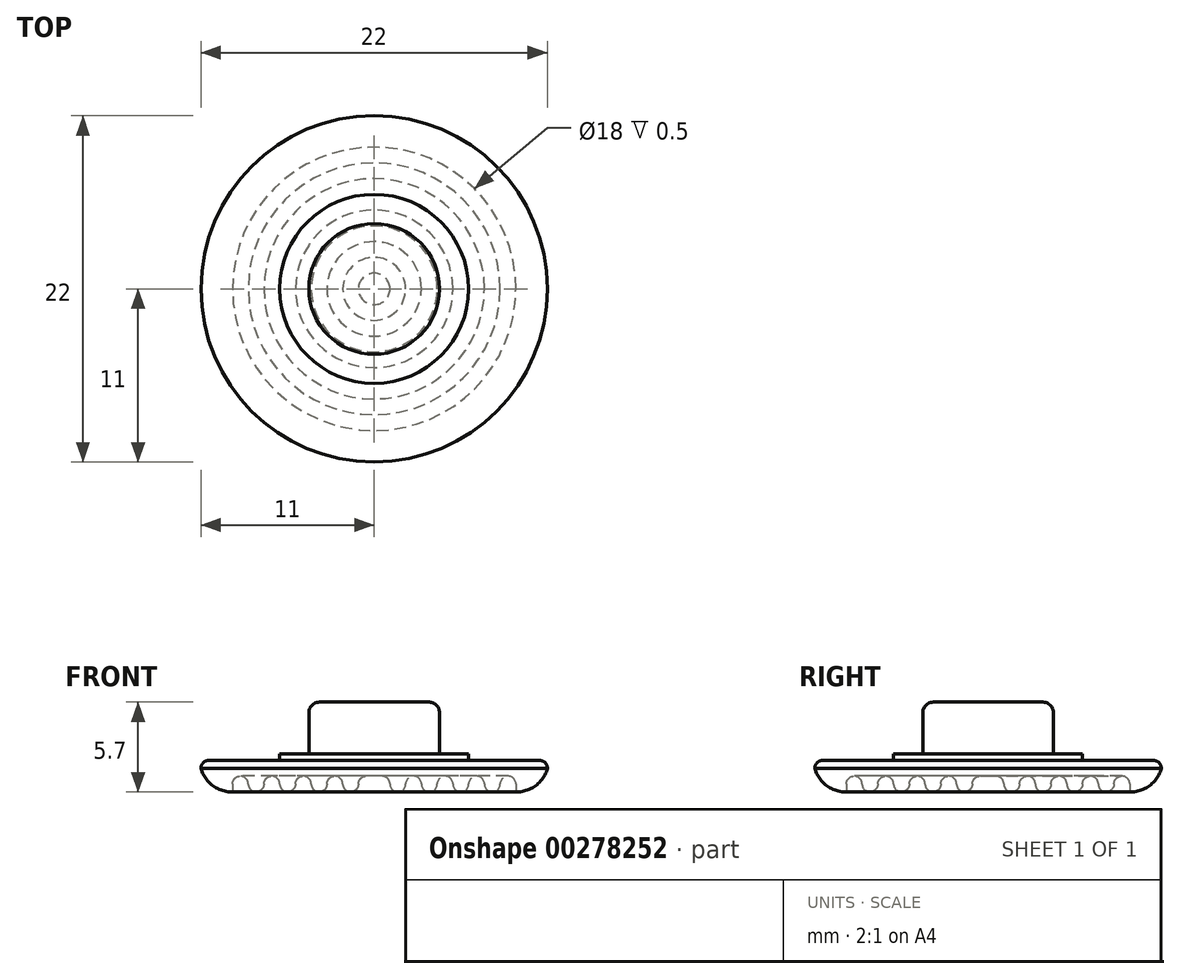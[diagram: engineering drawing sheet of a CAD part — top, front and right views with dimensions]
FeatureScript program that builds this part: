
annotation { "Feature Type Name" : "Feature", "Feature Type Description" : "" }
export const myFeature = defineFeature(function(context is Context, id is Id, definition is map)
    precondition{}
    {
        {
            var Q0;
            Q0=qCreatedBy(makeId("Top.planeOp"),FACE);
            var sketch = newSketch(context, id + "F0", { "sketchPlane" : qUnion([Q0])});
            skCircle(sketch, "E0", {"center": v(0, 0) * mm, "radius": 4.15 * mm});
            skCircle(sketch, "E1", {"center": v(0, 0) * mm, "radius": 11 * mm});
            skCircle(sketch, "E2", {"center": v(0, 0) * mm, "radius": 6 * mm});
            skSolve(sketch);
        }
        {
            var Q0;
            Q0=makeQuery(id+"F0.imprint","IMPRINT",FACE,{"disambiguationData":[TD([[makeQuery(id+"F0.imprint","IMPRINT",EDGE,{"derivedFrom":sQuery(id+"F0.wireOp",EDGE,"E0")}),-1.0]])]});
            var Q1;
            Q1=makeQuery(id+"F0.imprint","IMPRINT",FACE,{"disambiguationData":[TD([[makeQuery(id+"F0.imprint","IMPRINT",EDGE,{"derivedFrom":sQuery(id+"F0.wireOp",EDGE,"E0")}),1.0]])]});
            var Q2;
            Q2=makeQuery(id+"F0.imprint","IMPRINT",FACE,{"disambiguationData":[TD([[makeQuery(id+"F0.imprint","IMPRINT",EDGE,{"derivedFrom":sQuery(id+"F0.wireOp",EDGE,"E1")}),1.0]])]});
            extrude(context, id + "F1", {"entities" : qUnion([Q0, Q1, Q2]), "depth" : 2 * mm, "offsetDistance" : 25 * mm});
        }
        {
            var Q0;
            Q0=makeQuery(id+"F0.imprint","IMPRINT",FACE,{"disambiguationData":[TD([[makeQuery(id+"F0.imprint","IMPRINT",EDGE,{"derivedFrom":sQuery(id+"F0.wireOp",EDGE,"E0")}),1.0]])]});
            extrude(context, id + "F2", {"entities" : qUnion([Q0]), "operationType" : NewBodyOperationType.ADD, "depth" : 5.7 * mm, "offsetDistance" : 25 * mm});
        }
        {
            var Q0;
            Q0=makeQuery(id+"F1.opExtrude","CAP_EDGE",EDGE,{"disambiguationData":[OSD([sQuery(id+"F0.wireOp",EDGE,"E1")])],"isStart":false});
            fillet(context, id + "F3", {"entities" : qUnion([Q0]), "radius" : .5 * mm, "tangentPropagation" : true, "allowEdgeOverflow" : false});
        }
        {
            var Q0;
            Q0=makeQuery(id+"F1.opExtrude","CAP_EDGE",EDGE,{"disambiguationData":[OSD([sQuery(id+"F0.wireOp",EDGE,"E1")])],"isStart":true});
            fillet(context, id + "F4", {"entities" : qUnion([Q0]), "radius" : 2 * mm, "tangentPropagation" : true, "allowEdgeOverflow" : false});
        }
        {
            var Q0;
            Q0=makeQuery(id+"F0.imprint","IMPRINT",FACE,{"disambiguationData":[TD([[makeQuery(id+"F0.imprint","IMPRINT",EDGE,{"derivedFrom":sQuery(id+"F0.wireOp",EDGE,"E0")}),-1.0]])]});
            extrude(context, id + "F5", {"entities" : qUnion([Q0]), "operationType" : NewBodyOperationType.ADD, "depth" : 2.4 * mm, "offsetDistance" : 25 * mm});
        }
        {
            var Q0;
            Q0=qCreatedBy(makeId("Top.planeOp"),FACE);
            var sketch = newSketch(context, id + "F6", { "sketchPlane" : qUnion([Q0])});
            skCircle(sketch, "E3", {"center": v(0, 0) * mm, "radius": 11 * mm});
            skCircle(sketch, "E4", {"center": v(0, 0) * mm, "radius": 8 * mm});
            skCircle(sketch, "E5", {"center": v(0, 0) * mm, "radius": 7.5 * mm});
            skCircle(sketch, "E6", {"center": v(0, 0) * mm, "radius": 7 * mm});
            skCircle(sketch, "E7", {"center": v(0, 0) * mm, "radius": 6 * mm});
            skCircle(sketch, "E8", {"center": v(0, 0) * mm, "radius": 5.5 * mm});
            skCircle(sketch, "E9", {"center": v(0, 0) * mm, "radius": 5 * mm});
            skCircle(sketch, "E10", {"center": v(0, 0) * mm, "radius": 4.5 * mm});
            skCircle(sketch, "E11", {"center": v(0, 0) * mm, "radius": 4 * mm});
            skCircle(sketch, "E12", {"center": v(0, 0) * mm, "radius": 3.5 * mm});
            skCircle(sketch, "E13", {"center": v(0, 0) * mm, "radius": 3 * mm});
            skCircle(sketch, "E14", {"center": v(0, 0) * mm, "radius": 2.5 * mm});
            skCircle(sketch, "E15", {"center": v(0, 0) * mm, "radius": 2 * mm});
            skCircle(sketch, "E16", {"center": v(0, 0) * mm, "radius": 1.5 * mm});
            skCircle(sketch, "E17", {"center": v(0, 0) * mm, "radius": 1 * mm});
            skCircle(sketch, "E18", {"center": v(0, 0) * mm, "radius": 0.5 * mm});
            skCircle(sketch, "E19", {"center": v(0, 0) * mm, "radius": 6.5 * mm});
            skCircle(sketch, "E20", {"center": v(0, 0) * mm, "radius": 8.5 * mm});
            skCircle(sketch, "E21", {"center": v(0, 0) * mm, "radius": 9 * mm});
            skSolve(sketch);
        }
        {
            var Q0;
            Q0=makeQuery(id+"F6.imprint","IMPRINT",FACE,{"disambiguationData":[TD([[makeQuery(id+"F6.imprint","IMPRINT",EDGE,{"derivedFrom":sQuery(id+"F6.wireOp",EDGE,"E18")}),1.0]])]});
            var Q1;
            Q1=makeQuery(id+"F6.imprint","IMPRINT",FACE,{"disambiguationData":[TD([[makeQuery(id+"F6.imprint","IMPRINT",EDGE,{"derivedFrom":sQuery(id+"F6.wireOp",EDGE,"E14")}),1.0]])]});
            var Q2;
            Q2=makeQuery(id+"F6.imprint","IMPRINT",FACE,{"disambiguationData":[TD([[makeQuery(id+"F6.imprint","IMPRINT",EDGE,{"derivedFrom":sQuery(id+"F6.wireOp",EDGE,"E10")}),1.0]])]});
            var Q3;
            Q3=makeQuery(id+"F6.imprint","IMPRINT",FACE,{"disambiguationData":[TD([[makeQuery(id+"F6.imprint","IMPRINT",EDGE,{"derivedFrom":sQuery(id+"F6.wireOp",EDGE,"E7")}),-1.0]])]});
            var Q4;
            Q4=makeQuery(id+"F6.imprint","IMPRINT",FACE,{"disambiguationData":[TD([[makeQuery(id+"F6.imprint","IMPRINT",EDGE,{"derivedFrom":sQuery(id+"F6.wireOp",EDGE,"E17")}),1.0]])]});
            var Q5;
            Q5=makeQuery(id+"F6.imprint","IMPRINT",FACE,{"disambiguationData":[TD([[makeQuery(id+"F6.imprint","IMPRINT",EDGE,{"derivedFrom":sQuery(id+"F6.wireOp",EDGE,"E13")}),1.0]])]});
            var Q6;
            Q6=makeQuery(id+"F6.imprint","IMPRINT",FACE,{"disambiguationData":[TD([[makeQuery(id+"F6.imprint","IMPRINT",EDGE,{"derivedFrom":sQuery(id+"F6.wireOp",EDGE,"E9")}),1.0]])]});
            var Q7;
            Q7=makeQuery(id+"F6.imprint","IMPRINT",FACE,{"disambiguationData":[TD([[makeQuery(id+"F6.imprint","IMPRINT",EDGE,{"derivedFrom":sQuery(id+"F6.wireOp",EDGE,"E6")}),1.0]])]});
            var Q8;
            Q8=makeQuery(id+"F6.imprint","IMPRINT",FACE,{"disambiguationData":[TD([[makeQuery(id+"F6.imprint","IMPRINT",EDGE,{"derivedFrom":sQuery(id+"F6.wireOp",EDGE,"E20")}),-1.0]])]});
            var Q9;
            Q9=makeQuery(id+"F6.imprint","IMPRINT",FACE,{"disambiguationData":[TD([[makeQuery(id+"F6.imprint","IMPRINT",EDGE,{"derivedFrom":sQuery(id+"F6.wireOp",EDGE,"E4")}),-1.0]])]});
            extrude(context, id + "F7", {"entities" : qUnion([Q0, Q1, Q2, Q3, Q4, Q5, Q6, Q7, Q8, Q9]), "operationType" : NewBodyOperationType.REMOVE, "depth" : 1 * mm, "offsetDistance" : 25 * mm});
        }
        {
            var Q0;
            Q0=makeQuery(id+"F7.boolean.opBoolean","COPY",FACE,{"derivedFrom":makeQuery(id+"F7.opExtrude","CAP_FACE",FACE,{"disambiguationData":[OSD([sQuery(id+"F6.wireOp",EDGE,"E16"),sQuery(id+"F6.wireOp",EDGE,"E17")])],"isStart":false})});
            var Q1;
            Q1=makeQuery(id+"F7.boolean.opBoolean","COPY",FACE,{"derivedFrom":makeQuery(id+"F7.opExtrude","CAP_FACE",FACE,{"disambiguationData":[OSD([sQuery(id+"F6.wireOp",EDGE,"E14"),sQuery(id+"F6.wireOp",EDGE,"E15")])],"isStart":false})});
            var Q2;
            Q2=makeQuery(id+"F7.boolean.opBoolean","COPY",FACE,{"derivedFrom":makeQuery(id+"F7.opExtrude","CAP_FACE",FACE,{"disambiguationData":[OSD([sQuery(id+"F6.wireOp",EDGE,"E18")])],"isStart":false})});
            var Q3;
            Q3=makeQuery(id+"F7.boolean.opBoolean","COPY",FACE,{"derivedFrom":makeQuery(id+"F7.opExtrude","CAP_FACE",FACE,{"disambiguationData":[OSD([sQuery(id+"F6.wireOp",EDGE,"E12"),sQuery(id+"F6.wireOp",EDGE,"E13")])],"isStart":false})});
            var Q4;
            Q4=makeQuery(id+"F7.boolean.opBoolean","COPY",FACE,{"derivedFrom":makeQuery(id+"F7.opExtrude","CAP_FACE",FACE,{"disambiguationData":[OSD([sQuery(id+"F6.wireOp",EDGE,"E10"),sQuery(id+"F6.wireOp",EDGE,"E11")])],"isStart":false})});
            var Q5;
            Q5=makeQuery(id+"F7.boolean.opBoolean","COPY",FACE,{"derivedFrom":makeQuery(id+"F7.opExtrude","CAP_FACE",FACE,{"disambiguationData":[OSD([sQuery(id+"F6.wireOp",EDGE,"E8"),sQuery(id+"F6.wireOp",EDGE,"E9")])],"isStart":false})});
            var Q6;
            Q6=makeQuery(id+"F7.boolean.opBoolean","COPY",FACE,{"derivedFrom":makeQuery(id+"F7.opExtrude","CAP_FACE",FACE,{"disambiguationData":[OSD([sQuery(id+"F6.wireOp",EDGE,"E7"),sQuery(id+"F6.wireOp",EDGE,"E19")])],"isStart":false})});
            var Q7;
            Q7=makeQuery(id+"F7.boolean.opBoolean","COPY",FACE,{"derivedFrom":makeQuery(id+"F7.opExtrude","CAP_FACE",FACE,{"disambiguationData":[OSD([sQuery(id+"F6.wireOp",EDGE,"E5"),sQuery(id+"F6.wireOp",EDGE,"E6")])],"isStart":false})});
            var Q8;
            Q8=makeQuery(id+"F7.boolean.opBoolean","COPY",FACE,{"derivedFrom":makeQuery(id+"F7.opExtrude","CAP_FACE",FACE,{"disambiguationData":[OSD([sQuery(id+"F6.wireOp",EDGE,"E4"),sQuery(id+"F6.wireOp",EDGE,"E21")])],"isStart":false})});
            fillet(context, id + "F8", {"entities" : qUnion([Q0, Q1, Q2, Q3, Q4, Q5, Q6, Q7, Q8]), "radius" : .5 * mm, "tangentPropagation" : true, "allowEdgeOverflow" : false});
        }
        {
            var Q0;
            Q0=makeQuery(id+"F7.boolean.opBoolean","SPLIT",FACE,{"disambiguationData":[TD([makeQuery(id+"F7.opExtrude","SWEPT_FACE",FACE,{"disambiguationData":[OSD([sQuery(id+"F6.wireOp",EDGE,"E17")])]})])],"derivedFrom":makeQuery(id+"F1.opExtrude","CAP_FACE",FACE,{"disambiguationData":[OSD([sQuery(id+"F0.wireOp",EDGE,"E1")])],"isStart":true})});
            var Q1;
            Q1=makeQuery(id+"F7.boolean.opBoolean","SPLIT",FACE,{"disambiguationData":[TD([makeQuery(id+"F7.opExtrude","SWEPT_FACE",FACE,{"disambiguationData":[OSD([sQuery(id+"F6.wireOp",EDGE,"E15")])]})])],"derivedFrom":makeQuery(id+"F1.opExtrude","CAP_FACE",FACE,{"disambiguationData":[OSD([sQuery(id+"F0.wireOp",EDGE,"E1")])],"isStart":true})});
            var Q2;
            Q2=makeQuery(id+"F7.boolean.opBoolean","SPLIT",FACE,{"disambiguationData":[TD([makeQuery(id+"F7.opExtrude","SWEPT_FACE",FACE,{"disambiguationData":[OSD([sQuery(id+"F6.wireOp",EDGE,"E13")])]})])],"derivedFrom":makeQuery(id+"F1.opExtrude","CAP_FACE",FACE,{"disambiguationData":[OSD([sQuery(id+"F0.wireOp",EDGE,"E1")])],"isStart":true})});
            var Q3;
            Q3=makeQuery(id+"F7.boolean.opBoolean","SPLIT",FACE,{"disambiguationData":[TD([makeQuery(id+"F7.opExtrude","SWEPT_FACE",FACE,{"disambiguationData":[OSD([sQuery(id+"F6.wireOp",EDGE,"E11")])]})])],"derivedFrom":makeQuery(id+"F1.opExtrude","CAP_FACE",FACE,{"disambiguationData":[OSD([sQuery(id+"F0.wireOp",EDGE,"E1")])],"isStart":true})});
            var Q4;
            Q4=makeQuery(id+"F7.boolean.opBoolean","SPLIT",FACE,{"disambiguationData":[TD([makeQuery(id+"F7.opExtrude","SWEPT_FACE",FACE,{"disambiguationData":[OSD([sQuery(id+"F6.wireOp",EDGE,"E8")])]})])],"derivedFrom":makeQuery(id+"F1.opExtrude","CAP_FACE",FACE,{"disambiguationData":[OSD([sQuery(id+"F0.wireOp",EDGE,"E1")])],"isStart":true})});
            var Q5;
            Q5=makeQuery(id+"F7.boolean.opBoolean","SPLIT",FACE,{"disambiguationData":[TD([makeQuery(id+"F7.opExtrude","SWEPT_FACE",FACE,{"disambiguationData":[OSD([sQuery(id+"F6.wireOp",EDGE,"E6")])]})])],"derivedFrom":makeQuery(id+"F1.opExtrude","CAP_FACE",FACE,{"disambiguationData":[OSD([sQuery(id+"F0.wireOp",EDGE,"E1")])],"isStart":true})});
            var Q6;
            Q6=makeQuery(id+"F7.boolean.opBoolean","COPY",EDGE,{"derivedFrom":makeQuery(id+"F7.opExtrude","CAP_EDGE",EDGE,{"disambiguationData":[OSD([sQuery(id+"F6.wireOp",EDGE,"E5")])],"isStart":true})});
            var Q7;
            Q7=makeQuery(id+"F7.boolean.opBoolean","SPLIT",FACE,{"disambiguationData":[TD([makeQuery(id+"F7.opExtrude","SWEPT_FACE",FACE,{"disambiguationData":[OSD([sQuery(id+"F6.wireOp",EDGE,"E9")])]})])],"derivedFrom":makeQuery(id+"F1.opExtrude","CAP_FACE",FACE,{"disambiguationData":[OSD([sQuery(id+"F0.wireOp",EDGE,"E1")])],"isStart":true})});
            var Q8;
            Q8=makeQuery(id+"F7.boolean.opBoolean","COPY",EDGE,{"derivedFrom":makeQuery(id+"F7.opExtrude","CAP_EDGE",EDGE,{"disambiguationData":[OSD([sQuery(id+"F6.wireOp",EDGE,"E21")])],"isStart":true})});
            fillet(context, id + "F9", {"entities" : qUnion([Q0, Q1, Q2, Q3, Q4, Q5, Q6, Q7, Q8]), "radius" : .5 * mm, "tangentPropagation" : true, "allowEdgeOverflow" : false});
        }
        {
            var Q0;
            Q0=makeQuery(id+"F2.opExtrude","CAP_EDGE",EDGE,{"disambiguationData":[OSD([sQuery(id+"F0.wireOp",EDGE,"E0")])],"isStart":false});
            fillet(context, id + "F10", {"entities" : qUnion([Q0]), "radius" : 2 / 3 * mm, "tangentPropagation" : true, "allowEdgeOverflow" : false});
        }
    });
